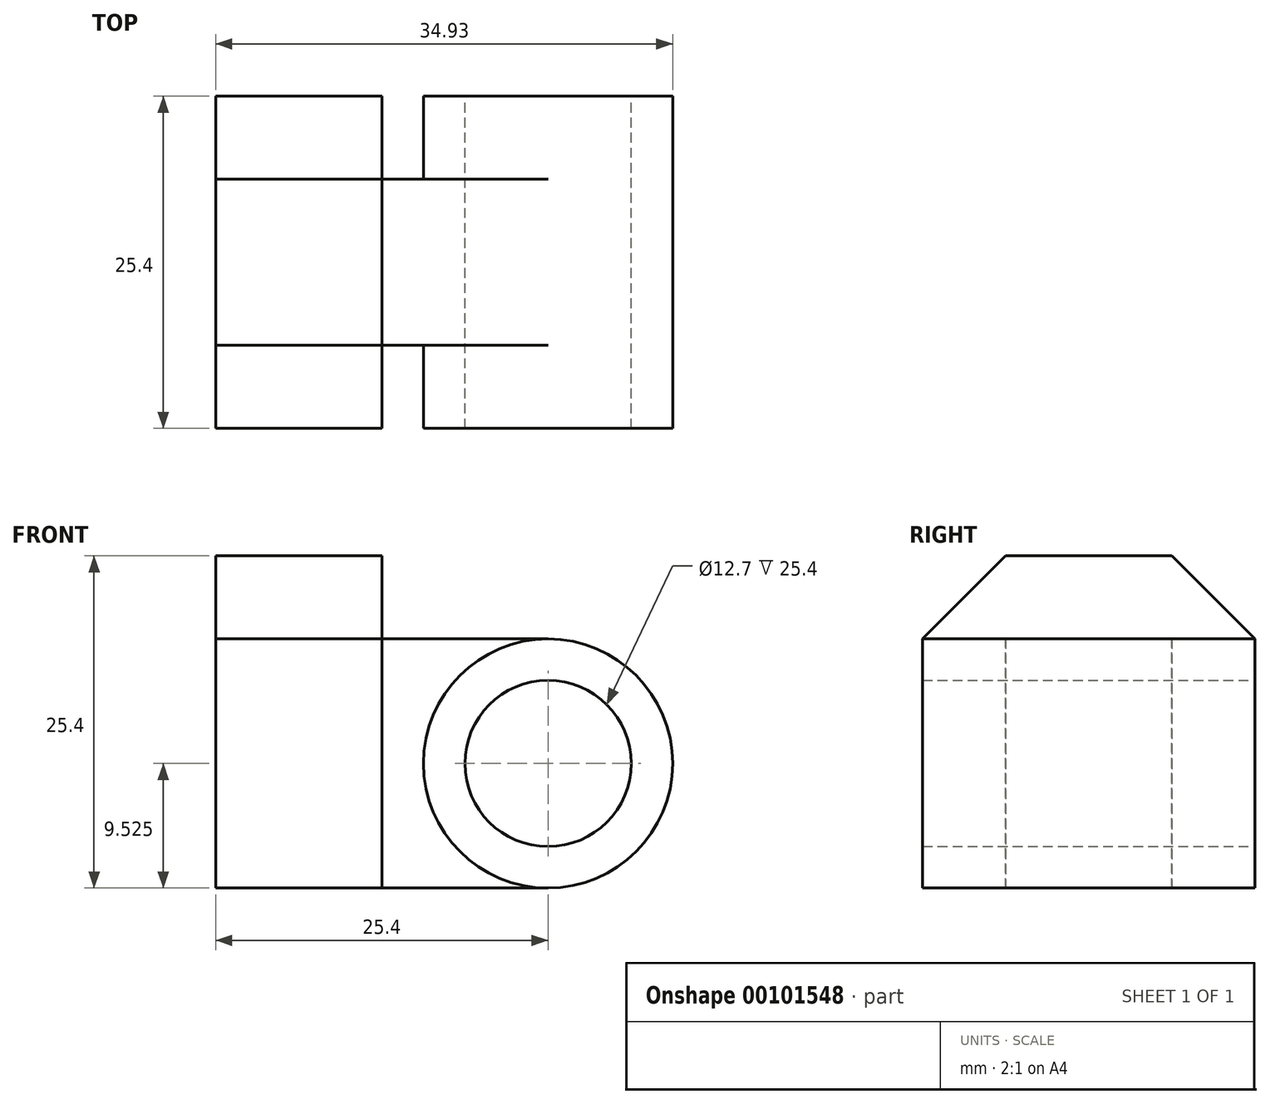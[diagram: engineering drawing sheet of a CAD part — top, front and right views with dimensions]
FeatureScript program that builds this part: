
annotation { "Feature Type Name" : "Feature", "Feature Type Description" : "" }
export const myFeature = defineFeature(function(context is Context, id is Id, definition is map)
    precondition{}
    {
        {
            var Q0;
            Q0=qCreatedBy(makeId("Front.planeOp"),FACE);
            var sketch = newSketch(context, id + "F0", { "sketchPlane" : qUnion([Q0])});
            skLineSegment(sketch, "E0", {"start": v(0, 0) * mm, "end": v(0, 19.05) * mm});
            skLineSegment(sketch, "E1", {"start": v(0, 19.05) * mm, "end": v(12.7, 19.05) * mm});
            skLineSegment(sketch, "E2", {"start": v(12.7, 0) * mm, "end": v(0, 0) * mm});
            skCircle(sketch, "E3", {"center": v(12.7, 9.53) * mm, "radius": 9.53 * mm});
            skCircle(sketch, "E4", {"center": v(12.7, 9.53) * mm, "radius": 6.35 * mm});
            skSolve(sketch);
        }
        {
            var Q0;
            Q0=makeQuery(id+"F0.imprint","IMPRINT",FACE,{"disambiguationData":[TD([[makeQuery(id+"F0.imprint","IMPRINT",EDGE,{"derivedFrom":sQuery(id+"F0.wireOp",EDGE,"E4")}),-1.0]])]});
            extrude(context, id + "F1", {"entities" : qUnion([Q0]), "endBound" : BoundingType.SYMMETRIC, "depth" : 25.4 * mm});
        }
        {
            var Q0;
            Q0=makeQuery(id+"F0.imprint","IMPRINT",FACE,{"disambiguationData":[TD([[makeQuery(id+"F0.imprint","IMPRINT",EDGE,{"derivedFrom":sQuery(id+"F0.wireOp",EDGE,"E0")}),-1.0]])]});
            extrude(context, id + "F2", {"entities" : qUnion([Q0]), "operationType" : NewBodyOperationType.ADD, "endBound" : BoundingType.SYMMETRIC, "depth" : 12.7 * mm});
        }
        {
            var Q0;
            Q0=qCreatedBy(makeId("Front.planeOp"),FACE);
            var sketch = newSketch(context, id + "F3", { "sketchPlane" : qUnion([Q0])});
            skLineSegment(sketch, "E5.bottom", {"start": v(0, 0) * mm, "end": v(-12.7, 0) * mm});
            skLineSegment(sketch, "E5.top", {"start": v(0, 25.4) * mm, "end": v(-12.7, 25.4) * mm});
            skLineSegment(sketch, "E5.left", {"start": v(0, 0) * mm, "end": v(0, 25.4) * mm});
            skLineSegment(sketch, "E5.right", {"start": v(-12.7, 0) * mm, "end": v(-12.7, 25.4) * mm});
            skSolve(sketch);
        }
        {
            var Q0;
            Q0 = qSketchRegion(id + "FcjUotcVo6P4dLD_2", true);
            var Q1;
            Q1=makeQuery(id+"F3.imprint","IMPRINT",FACE,{"disambiguationData":[TD([[makeQuery(id+"F3.imprint","IMPRINT",EDGE,{"derivedFrom":sQuery(id+"F3.wireOp",EDGE,"E5.bottom")}),-1.0]])]});
            extrude(context, id + "F4", {"entities" : qUnion([Q0, Q1]), "operationType" : NewBodyOperationType.ADD, "endBound" : BoundingType.SYMMETRIC, "depth" : 25.4 * mm});
        }
        {
            var Q0;
            Q0=makeQuery(id+"F4.opExtrude","SWEPT_FACE",FACE,{"disambiguationData":[OSD([sQuery(id+"F3.wireOp",EDGE,"E5.right")])]});
            var sketch = newSketch(context, id + "F5", { "sketchPlane" : qUnion([Q0])});
            skLineSegment(sketch, "E6", {"start": v(-12.7, 19.05) * mm, "end": v(-6.35, 25.4) * mm});
            skLineSegment(sketch, "E7", {"start": v(6.35, 25.4) * mm, "end": v(12.7, 19.05) * mm});
            skSolve(sketch);
        }
        {
            var Q0;
            {var subQ0=sQuery(id+"F5.wireOp",EDGE,"E6");Q0=makeQuery(id+"F5.imprint","IMPRINT",FACE,{"disambiguationData":[TD([[makeQuery(id+"F5.imprint","IMPRINT",EDGE,{"derivedFrom":subQ0}),1.0]])]});}
            var Q1;
            {var subQ0=sQuery(id+"F5.wireOp",EDGE,"E7");Q1=makeQuery(id+"F5.imprint","IMPRINT",FACE,{"disambiguationData":[TD([[makeQuery(id+"F5.imprint","IMPRINT",EDGE,{"derivedFrom":subQ0}),1.0]])]});}
            extrude(context, id + "F6", {"entities" : qUnion([Q0, Q1]), "operationType" : NewBodyOperationType.REMOVE, "endBound" : BoundingType.THROUGH_ALL, "oppositeDirection" : true, "depth" : 25.4 * mm});
        }
    });
